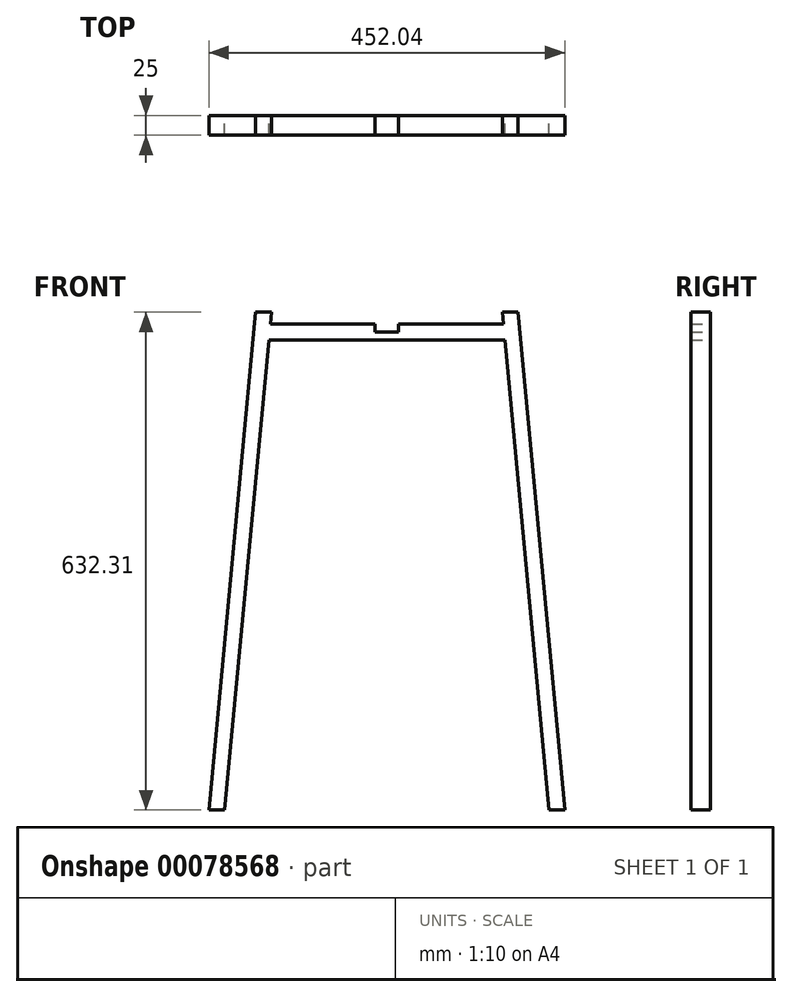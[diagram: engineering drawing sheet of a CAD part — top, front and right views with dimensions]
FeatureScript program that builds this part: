
annotation { "Feature Type Name" : "Feature", "Feature Type Description" : "" }
export const myFeature = defineFeature(function(context is Context, id is Id, definition is map)
    precondition{}
    {
        {
            var Q0;
            Q0=qCreatedBy(makeId("Front.planeOp"),FACE);
            var sketch = newSketch(context, id + "F0", { "sketchPlane" : qUnion([Q0])});
            skLineSegment(sketch, "E0", {"start": v(0, 0) * mm, "end": v(-150, 0) * mm});
            skLineSegment(sketch, "E1", {"start": v(-150, 0) * mm, "end": v(-206.02, -597.38) * mm});
            skLineSegment(sketch, "E2", {"start": v(-206.02, -597.38) * mm, "end": v(-226.02, -597.38) * mm});
            skLineSegment(sketch, "E3", {"start": v(-226.02, -597.38) * mm, "end": v(-166.72, 34.93) * mm});
            skLineSegment(sketch, "E4", {"start": v(-206.02, -597.38) * mm, "end": v(-140.62, 100.06) * mm, "construction": true});
            skLineSegment(sketch, "E5", {"start": v(-166.72, 34.93) * mm, "end": v(-146.72, 34.93) * mm, "construction": true});
            skLineSegment(sketch, "E6", {"start": v(0, 0) * mm, "end": v(0, 20) * mm, "construction": true});
            skLineSegment(sketch, "E7", {"start": v(0, 20) * mm, "end": v(-148.12, 20) * mm});
            skLineSegment(sketch, "E8", {"start": v(-148.12, 20) * mm, "end": v(-146.72, 34.93) * mm});
            skLineSegment(sketch, "E9", {"start": v(-146.72, 34.93) * mm, "end": v(-166.72, 34.93) * mm});
            skLineSegment(sketch, "E10.MirrorCS", {"start": v(166.72, 34.93) * mm, "end": v(146.72, 34.93) * mm, "construction": true});
            skLineSegment(sketch, "E11.MirrorCS", {"start": v(148.12, 20) * mm, "end": v(146.72, 34.93) * mm});
            skLineSegment(sketch, "E12.MirrorCS", {"start": v(146.72, 34.93) * mm, "end": v(166.72, 34.93) * mm});
            skLineSegment(sketch, "E13.MirrorCS", {"start": v(206.02, -597.38) * mm, "end": v(226.02, -597.38) * mm});
            skLineSegment(sketch, "E14.MirrorCS", {"start": v(206.02, -597.38) * mm, "end": v(140.62, 100.06) * mm, "construction": true});
            skLineSegment(sketch, "E15.MirrorCS", {"start": v(150, 0) * mm, "end": v(206.02, -597.38) * mm});
            skLineSegment(sketch, "E16.MirrorCS", {"start": v(226.02, -597.38) * mm, "end": v(166.72, 34.93) * mm});
            skLineSegment(sketch, "E17.MirrorCS", {"start": v(0, 0) * mm, "end": v(150, 0) * mm});
            skLineSegment(sketch, "E18.MirrorCS", {"start": v(0, 20) * mm, "end": v(148.12, 20) * mm});
            skLineSegment(sketch, "E19.bottom", {"start": v(-15.34, 20) * mm, "end": v(14.66, 20) * mm});
            skLineSegment(sketch, "E20.bottom", {"start": v(0, 20) * mm, "end": v(-15, 20) * mm});
            skLineSegment(sketch, "E20.top", {"start": v(0, 10) * mm, "end": v(-15, 10) * mm});
            skLineSegment(sketch, "E20.left", {"start": v(0, 20) * mm, "end": v(0, 10) * mm});
            skLineSegment(sketch, "E20.right", {"start": v(-15, 20) * mm, "end": v(-15, 10) * mm});
            skLineSegment(sketch, "E21.bottom", {"start": v(0, 10) * mm, "end": v(15, 10) * mm});
            skLineSegment(sketch, "E21.top", {"start": v(0, 20) * mm, "end": v(15, 20) * mm});
            skLineSegment(sketch, "E21.left", {"start": v(0, 10) * mm, "end": v(0, 20) * mm});
            skLineSegment(sketch, "E21.right", {"start": v(15, 10) * mm, "end": v(15, 20) * mm});
            skSolve(sketch);
        }
        {
            var Q0;
            Q0=makeQuery(id+"F0.imprint","IMPRINT",FACE,{"disambiguationData":[TD([[makeQuery(id+"F0.imprint","IMPRINT",EDGE,{"derivedFrom":sQuery(id+"F0.wireOp",EDGE,"E0")}),-1.0]])]});
            extrude(context, id + "F1", {"entities" : qUnion([Q0]), "depth" : 25 * mm});
        }
    });
